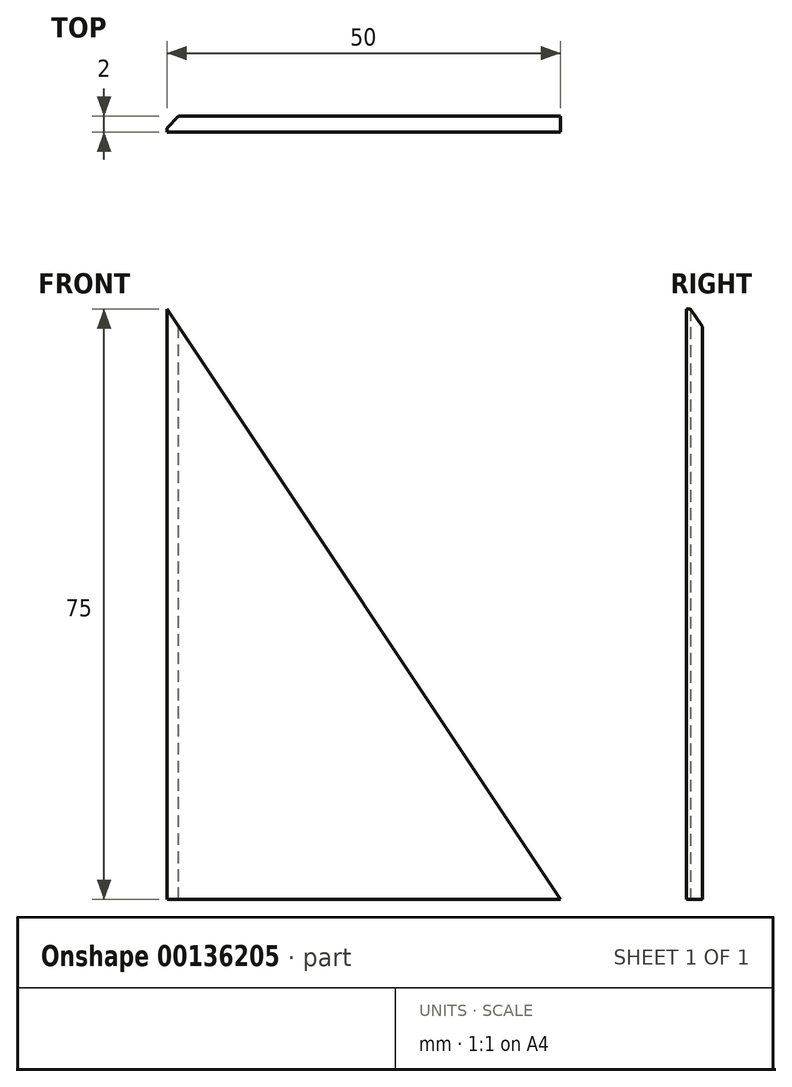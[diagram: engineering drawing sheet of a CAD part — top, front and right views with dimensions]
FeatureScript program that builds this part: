
annotation { "Feature Type Name" : "Feature", "Feature Type Description" : "" }
export const myFeature = defineFeature(function(context is Context, id is Id, definition is map)
    precondition{}
    {
        {
            var Q0;
            Q0=qCreatedBy(makeId("Front.planeOp"),FACE);
            var sketch = newSketch(context, id + "F0", { "sketchPlane" : qUnion([Q0])});
            skLineSegment(sketch, "E0", {"start": v(-50, 0) * mm, "end": v(0, 0) * mm});
            skLineSegment(sketch, "E1", {"start": v(0, 0) * mm, "end": v(-50, 75) * mm});
            skLineSegment(sketch, "E2", {"start": v(-50, 75) * mm, "end": v(-50, 0) * mm});
            skSolve(sketch);
        }
        {
            var Q0;
            Q0 = qSketchRegion(id + "F0", true);
            extrude(context, id + "F1", {"entities" : qUnion([Q0]), "depth" : 2 * mm});
        }
        {
            var Q0;
            Q0=makeQuery(id+"F1.opExtrude","CAP_EDGE",EDGE,{"disambiguationData":[OSD([sQuery(id+"F0.wireOp",EDGE,"E2")])],"isStart":true});
            chamfer(context, id + "F2", {"entities" : qUnion([Q0]), "width" : 1.5 * mm, "tangentPropagation" : true});
        }
    });
